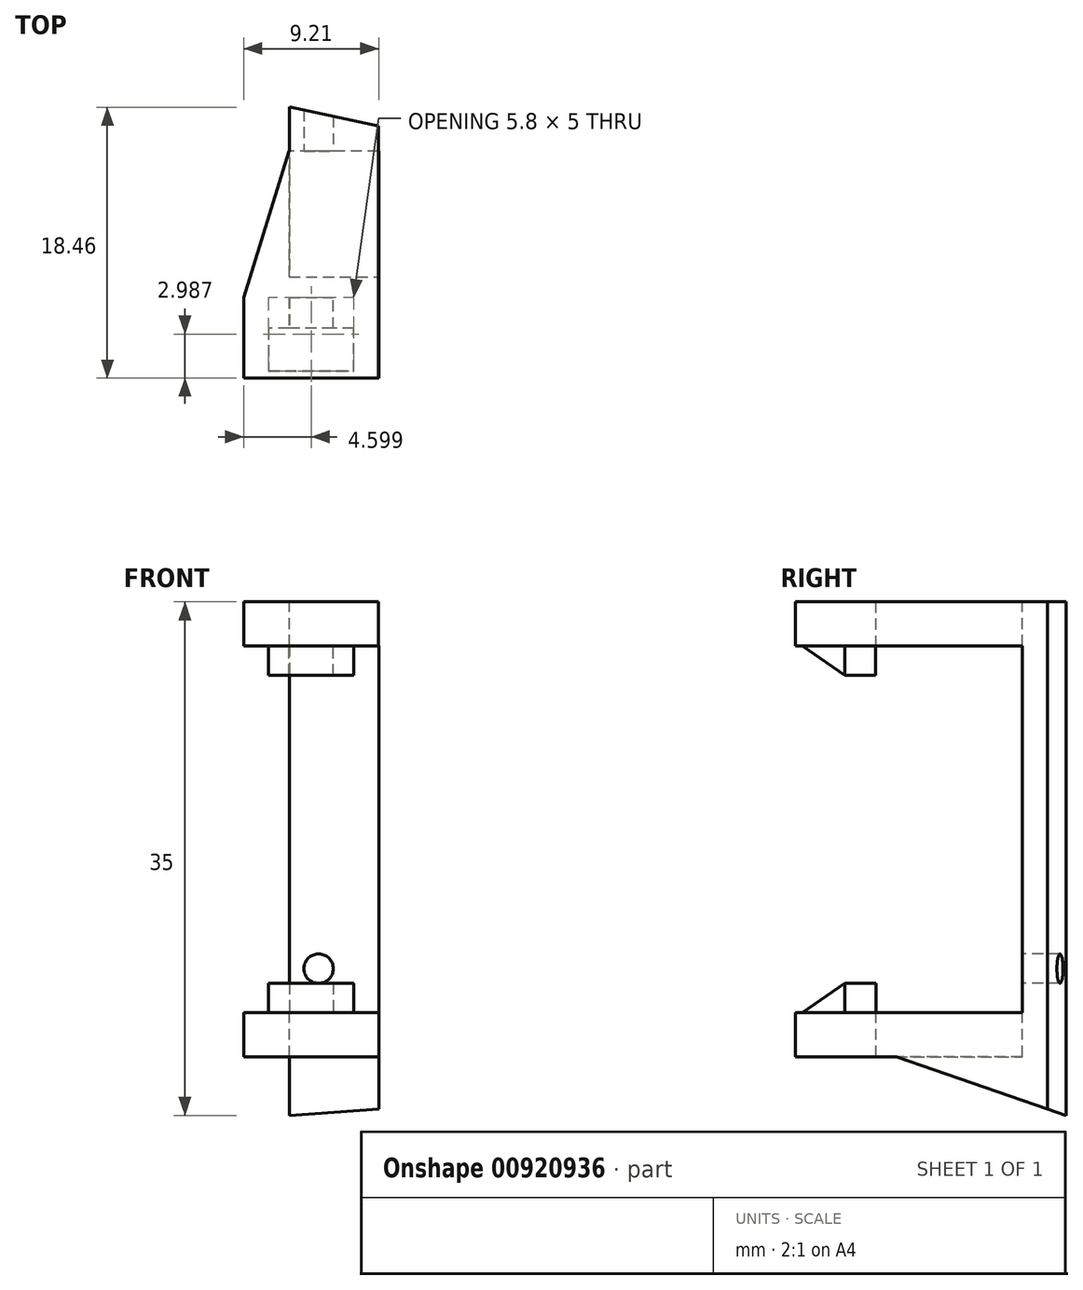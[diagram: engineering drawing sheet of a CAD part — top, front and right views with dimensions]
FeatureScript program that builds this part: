
annotation { "Feature Type Name" : "Feature", "Feature Type Description" : "" }
export const myFeature = defineFeature(function(context is Context, id is Id, definition is map)
    precondition{}
    {
        {
            var Q0;
            Q0=qCreatedBy(makeId("Top.planeOp"),FACE);
            var sketch = newSketch(context, id + "F0", { "sketchPlane" : qUnion([Q0])});
            skLineSegment(sketch, "E0", {"start": v(-27.76, 10.42) * mm, "end": v(-27.76, 8.32) * mm});
            skLineSegment(sketch, "E1", {"start": v(-27.76, 8.32) * mm, "end": v(-29.16, 8.32) * mm});
            skLineSegment(sketch, "E2", {"start": v(-29.16, 8.32) * mm, "end": v(-29.16, 5.42) * mm});
            skLineSegment(sketch, "E3", {"start": v(-29.16, 5.42) * mm, "end": v(-23.36, 5.42) * mm});
            skLineSegment(sketch, "E4", {"start": v(-23.36, 5.42) * mm, "end": v(-23.36, 8.32) * mm});
            skLineSegment(sketch, "E5", {"start": v(-23.36, 8.32) * mm, "end": v(-24.76, 8.32) * mm});
            skLineSegment(sketch, "E6", {"start": v(-24.76, 8.32) * mm, "end": v(-24.76, 10.42) * mm});
            skLineSegment(sketch, "E7", {"start": v(-21.66, 4.93) * mm, "end": v(-21.66, 23.4) * mm});
            skLineSegment(sketch, "E8", {"start": v(-21.66, 23.4) * mm, "end": v(-27.76, 23.4) * mm});
            skLineSegment(sketch, "E9", {"start": v(-30.86, 10.42) * mm, "end": v(-30.86, 4.93) * mm});
            skPoint(sketch, "E10.start.orphan", {"position": v(-27.76, 16.38) * mm});
            skLineSegment(sketch, "E11", {"start": v(-27.76, 10.42) * mm, "end": v(-24.76, 10.42) * mm});
            skLineSegment(sketch, "E12", {"start": v(-30.86, 6.77) * mm, "end": v(-29.16, 6.77) * mm, "construction": true});
            skLineSegment(sketch, "E13", {"start": v(-21.66, 6.9) * mm, "end": v(-23.36, 6.9) * mm, "construction": true});
            skLineSegment(sketch, "E14", {"start": v(-27.76, 23.4) * mm, "end": v(-27.76, 20.4) * mm});
            skLineSegment(sketch, "E15", {"start": v(-27.76, 20.4) * mm, "end": v(-30.86, 10.42) * mm});
            skLineSegment(sketch, "E16", {"start": v(-21.66, 20.4) * mm, "end": v(-27.76, 20.4) * mm});
            skLineSegment(sketch, "E17", {"start": v(-24.1, 20.4) * mm, "end": v(-24.1, 23.4) * mm, "construction": true});
            skLineSegment(sketch, "E18", {"start": v(-25.84, 10.42) * mm, "end": v(-25.84, 20.4) * mm, "construction": true});
            skPoint(sketch, "E19.start.orphan", {"position": v(-30.7, 4.93) * mm});
            skLineSegment(sketch, "E20", {"start": v(-30.86, 4.93) * mm, "end": v(-21.66, 4.93) * mm});
            skSolve(sketch);
        }
        {
            var Q0;
            {var subQ0=sQuery(id+"F0.wireOp",EDGE,"E8");Q0=makeQuery(id+"F0.imprint","IMPRINT",FACE,{"disambiguationData":[TD([[makeQuery(id+"F0.imprint","IMPRINT",EDGE,{"derivedFrom":subQ0}),1.0]])]});}
            extrude(context, id + "F1", {"entities" : qUnion([Q0]), "depth" : 25 * mm, "offsetDistance" : 25 * mm});
        }
        {
            var Q0;
            Q0=makeQuery(id+"F1.opExtrude","CAP_FACE",FACE,{"disambiguationData":[OSD([sQuery(id+"F0.wireOp",EDGE,"E7"),sQuery(id+"F0.wireOp",EDGE,"E8"),sQuery(id+"F0.wireOp",EDGE,"E14"),sQuery(id+"F0.wireOp",EDGE,"E16")])],"isStart":false});
            var sketch = newSketch(context, id + "F2", { "sketchPlane" : qUnion([Q0])});
            skLineSegment(sketch, "E21", {"start": v(-27.77, 10.42) * mm, "end": v(-27.77, 8.32) * mm});
            skLineSegment(sketch, "E22", {"start": v(-27.77, 8.32) * mm, "end": v(-29.17, 8.32) * mm});
            skLineSegment(sketch, "E23", {"start": v(-29.17, 8.32) * mm, "end": v(-29.17, 5.42) * mm});
            skLineSegment(sketch, "E24", {"start": v(-29.17, 5.42) * mm, "end": v(-23.37, 5.42) * mm});
            skLineSegment(sketch, "E25", {"start": v(-23.37, 5.42) * mm, "end": v(-23.37, 8.32) * mm});
            skLineSegment(sketch, "E26", {"start": v(-23.37, 8.32) * mm, "end": v(-24.77, 8.32) * mm});
            skLineSegment(sketch, "E27", {"start": v(-24.77, 8.32) * mm, "end": v(-24.77, 10.42) * mm});
            skLineSegment(sketch, "E28", {"start": v(-21.67, 4.93) * mm, "end": v(-21.67, 23.4) * mm});
            skLineSegment(sketch, "E29", {"start": v(-21.67, 23.4) * mm, "end": v(-27.77, 23.4) * mm});
            skLineSegment(sketch, "E30", {"start": v(-30.87, 10.42) * mm, "end": v(-30.87, 4.93) * mm});
            skPoint(sketch, "E31.start.orphan", {"position": v(-27.77, 16.38) * mm});
            skLineSegment(sketch, "E32", {"start": v(-27.77, 10.42) * mm, "end": v(-24.77, 10.42) * mm});
            skLineSegment(sketch, "E33", {"start": v(-30.87, 6.76) * mm, "end": v(-29.17, 6.76) * mm, "construction": true});
            skLineSegment(sketch, "E34", {"start": v(-21.67, 6.9) * mm, "end": v(-23.37, 6.9) * mm, "construction": true});
            skLineSegment(sketch, "E35", {"start": v(-27.77, 23.4) * mm, "end": v(-27.77, 20.4) * mm});
            skLineSegment(sketch, "E36", {"start": v(-27.77, 20.4) * mm, "end": v(-30.87, 10.42) * mm});
            skLineSegment(sketch, "E37", {"start": v(-21.67, 20.4) * mm, "end": v(-27.77, 20.4) * mm});
            skLineSegment(sketch, "E38", {"start": v(-24.12, 20.4) * mm, "end": v(-24.12, 23.4) * mm, "construction": true});
            skLineSegment(sketch, "E39", {"start": v(-25.85, 10.42) * mm, "end": v(-25.85, 20.4) * mm, "construction": true});
            skPoint(sketch, "E40.end.orphan", {"position": v(-30.7, 4.93) * mm});
            skLineSegment(sketch, "E41", {"start": v(-30.87, 4.93) * mm, "end": v(-21.67, 4.93) * mm});
            skSolve(sketch);
        }
        {
            var Q0;
            Q0=makeQuery(id+"F2.imprint","IMPRINT",FACE,{"disambiguationData":[TD([[makeQuery(id+"F2.imprint","IMPRINT",EDGE,{"derivedFrom":sQuery(id+"F2.wireOp",EDGE,"E21")}),-1.0]])]});
            var Q1;
            {var subQ0=sQuery(id+"F2.wireOp",EDGE,"E29");var subQ1=sQuery(id+"F2.wireOp",EDGE,"E28");var subQ2=makeQuery(id+"F2.imprint","INTERSECT",VERTEX,{"derivedFrom":[subQ1,subQ0]});Q1=makeQuery(id+"F2.imprint","IMPRINT",FACE,{"disambiguationData":[TD([[makeQuery(id+"F2.imprint","IMPRINT",EDGE,{"disambiguationData":[TD([[subQ2,1.0]])],"derivedFrom":subQ1}),1.0]])]});}
            var Q2;
            Q2=makeQuery(id+"F2.imprint","IMPRINT",FACE,{"disambiguationData":[TD([[makeQuery(id+"F2.imprint","IMPRINT",EDGE,{"derivedFrom":sQuery(id+"F2.wireOp",EDGE,"E21")}),1.0]])]});
            extrude(context, id + "F3", {"entities" : qUnion([Q0, Q1, Q2]), "operationType" : NewBodyOperationType.ADD, "depth" : 3 * mm, "offsetDistance" : 25 * mm});
        }
        {
            var Q0;
            Q0=makeQuery(id+"F2.imprint","IMPRINT",FACE,{"disambiguationData":[TD([[makeQuery(id+"F2.imprint","IMPRINT",EDGE,{"derivedFrom":sQuery(id+"F2.wireOp",EDGE,"E21")}),1.0]])]});
            extrude(context, id + "F4", {"entities" : qUnion([Q0]), "operationType" : NewBodyOperationType.ADD, "oppositeDirection" : true, "depth" : 2 * mm, "offsetDistance" : 25 * mm});
        }
        {
            var Q0;
            Q0=makeQuery(id+"F0.imprint","IMPRINT",FACE,{"disambiguationData":[TD([[makeQuery(id+"F0.imprint","IMPRINT",EDGE,{"derivedFrom":sQuery(id+"F0.wireOp",EDGE,"E0")}),-1.0]])]});
            var Q1;
            {var subQ0=sQuery(id+"F0.wireOp",EDGE,"E8");Q1=makeQuery(id+"F0.imprint","IMPRINT",FACE,{"disambiguationData":[TD([[makeQuery(id+"F0.imprint","IMPRINT",EDGE,{"derivedFrom":subQ0}),1.0]])]});}
            var Q2;
            Q2=makeQuery(id+"F0.imprint","IMPRINT",FACE,{"disambiguationData":[TD([[makeQuery(id+"F0.imprint","IMPRINT",EDGE,{"derivedFrom":sQuery(id+"F0.wireOp",EDGE,"E0")}),1.0]])]});
            extrude(context, id + "F5", {"entities" : qUnion([Q0, Q1, Q2]), "operationType" : NewBodyOperationType.ADD, "oppositeDirection" : true, "depth" : 3 * mm, "offsetDistance" : 25 * mm});
        }
        {
            var Q0;
            Q0=makeQuery(id+"F0.imprint","IMPRINT",FACE,{"disambiguationData":[TD([[makeQuery(id+"F0.imprint","IMPRINT",EDGE,{"derivedFrom":sQuery(id+"F0.wireOp",EDGE,"E0")}),1.0]])]});
            extrude(context, id + "F6", {"entities" : qUnion([Q0]), "operationType" : NewBodyOperationType.ADD, "depth" : 2 * mm, "offsetDistance" : 25 * mm});
        }
        {
            var Q0;
            Q0=makeQuery(id+"F6.opExtrude","SWEPT_FACE",FACE,{"disambiguationData":[OSD([sQuery(id+"F0.wireOp",EDGE,"E2")])]});
            var sketch = newSketch(context, id + "F7", { "sketchPlane" : qUnion([Q0])});
            skLineSegment(sketch, "E42", {"start": v(-8.32, 2) * mm, "end": v(-5.42, 0) * mm});
            skLineSegment(sketch, "E43", {"start": v(-5.42, 0) * mm, "end": v(-5.42, 2) * mm});
            skLineSegment(sketch, "E44", {"start": v(-5.42, 2) * mm, "end": v(-8.32, 2) * mm});
            skSolve(sketch);
        }
        {
            var Q0;
            Q0=makeQuery(id+"F4.opExtrude","SWEPT_FACE",FACE,{"disambiguationData":[OSD([sQuery(id+"F2.wireOp",EDGE,"E23")])]});
            var sketch = newSketch(context, id + "F8", { "sketchPlane" : qUnion([Q0])});
            skLineSegment(sketch, "E45", {"start": v(-8.32, 23) * mm, "end": v(-5.42, 23) * mm});
            skLineSegment(sketch, "E46", {"start": v(-5.42, 23) * mm, "end": v(-5.42, 25) * mm});
            skLineSegment(sketch, "E47", {"start": v(-5.42, 25) * mm, "end": v(-8.32, 23) * mm});
            skSolve(sketch);
        }
        {
            var Q0;
            Q0=makeQuery(id+"F7.imprint","IMPRINT",FACE,{"disambiguationData":[TD([[makeQuery(id+"F7.imprint","IMPRINT",EDGE,{"derivedFrom":sQuery(id+"F7.wireOp",EDGE,"E42")}),1.0]])]});
            extrude(context, id + "F9", {"entities" : qUnion([Q0]), "operationType" : NewBodyOperationType.REMOVE, "oppositeDirection" : true, "depth" : 25 * mm, "offsetDistance" : 25 * mm});
        }
        {
            var Q0;
            Q0=makeQuery(id+"F8.imprint","IMPRINT",FACE,{"disambiguationData":[TD([[makeQuery(id+"F8.imprint","IMPRINT",EDGE,{"derivedFrom":sQuery(id+"F8.wireOp",EDGE,"E45")}),1.0]])]});
            extrude(context, id + "F10", {"entities" : qUnion([Q0]), "operationType" : NewBodyOperationType.REMOVE, "oppositeDirection" : true, "depth" : 25 * mm, "offsetDistance" : 25 * mm});
        }
        {
            var Q0;
            {var subQ0=sQuery(id+"F0.wireOp",EDGE,"E7");Q0=makeQuery(id+"F5.boolean.opBoolean","MERGE",FACE,{"derivedFrom":[makeQuery(id+"F1.opExtrude","SWEPT_FACE",FACE,{"disambiguationData":[OSD([subQ0])]}),makeQuery(id+"F5.opExtrude","SWEPT_FACE",FACE,{"disambiguationData":[OSD([subQ0])]})]});}
            var sketch = newSketch(context, id + "F11", { "sketchPlane" : qUnion([Q0])});
            skLineSegment(sketch, "E48", {"start": v(23.4, -3) * mm, "end": v(23.4, -7) * mm});
            skLineSegment(sketch, "E49", {"start": v(23.4, -7) * mm, "end": v(11.82, -3) * mm});
            skLineSegment(sketch, "E50", {"start": v(11.82, -3) * mm, "end": v(23.4, -3) * mm});
            skSolve(sketch);
        }
        {
            var Q0;
            Q0=makeQuery(id+"F11.imprint","IMPRINT",FACE,{"disambiguationData":[TD([[makeQuery(id+"F11.imprint","IMPRINT",EDGE,{"derivedFrom":sQuery(id+"F11.wireOp",EDGE,"E48")}),-1.0]])]});
            extrude(context, id + "F12", {"entities" : qUnion([Q0]), "operationType" : NewBodyOperationType.ADD, "oppositeDirection" : true, "depth" : 6.1 * mm, "offsetDistance" : 25 * mm});
        }
        {
            var Q0;
            {var subQ0=sQuery(id+"F2.wireOp",EDGE,"E28");Q0=makeQuery(id+"F3.boolean.opBoolean","MERGE",FACE,{"derivedFrom":[makeQuery(id+"F3.opExtrude","CAP_FACE",FACE,{"disambiguationData":[OSD([subQ0,sQuery(id+"F2.wireOp",EDGE,"E30"),sQuery(id+"F2.wireOp",EDGE,"E36"),sQuery(id+"F2.wireOp",EDGE,"E37"),sQuery(id+"F2.wireOp",EDGE,"E41")])],"isStart":false}),makeQuery(id+"F3.opExtrude","CAP_FACE",FACE,{"disambiguationData":[OSD([sQuery(id+"F0.wireOp",EDGE,"E14"),sQuery(id+"F0.wireOp",EDGE,"E16"),subQ0,sQuery(id+"F2.wireOp",EDGE,"E29")])],"isStart":false})]});}
            var sketch = newSketch(context, id + "F13", { "sketchPlane" : qUnion([Q0])});
            skLineSegment(sketch, "E51", {"start": v(-27.76, 23.4) * mm, "end": v(-21.67, 22.11) * mm});
            skLineSegment(sketch, "E52", {"start": v(-21.67, 22.11) * mm, "end": v(-21.67, 23.4) * mm});
            skLineSegment(sketch, "E53", {"start": v(-21.67, 23.4) * mm, "end": v(-27.76, 23.4) * mm});
            skSolve(sketch);
        }
        {
            var Q0;
            Q0=makeQuery(id+"F13.imprint","IMPRINT",FACE,{"disambiguationData":[TD([[makeQuery(id+"F13.imprint","IMPRINT",EDGE,{"derivedFrom":sQuery(id+"F13.wireOp",EDGE,"E51")}),1.0]])]});
            extrude(context, id + "F14", {"entities" : qUnion([Q0]), "operationType" : NewBodyOperationType.REMOVE, "oppositeDirection" : true, "depth" : 37.75 * mm, "offsetDistance" : 25 * mm});
        }
        {
            var Q0;
            Q0=makeQuery(id+"F1.opExtrude","SWEPT_FACE",FACE,{"disambiguationData":[OSD([sQuery(id+"F0.wireOp",EDGE,"E16")])]});
            var sketch = newSketch(context, id + "F15", { "sketchPlane" : qUnion([Q0])});
            skLineSegment(sketch, "E54", {"start": v(-25.76, 0) * mm, "end": v(-25.76, 3) * mm, "construction": true});
            skLineSegment(sketch, "E55", {"start": v(-25.76, 3) * mm, "end": v(-27.76, 3) * mm, "construction": true});
            skCircle(sketch, "E56", {"center": v(-25.76, 3) * mm, "radius": 1 * mm});
            skSolve(sketch);
        }
        {
            var Q0;
            Q0=makeQuery(id+"F15.imprint","IMPRINT",FACE,{"disambiguationData":[TD([[makeQuery(id+"F15.imprint","IMPRINT",EDGE,{"derivedFrom":sQuery(id+"F15.wireOp",EDGE,"E56")}),1.0]])]});
            extrude(context, id + "F16", {"entities" : qUnion([Q0]), "operationType" : NewBodyOperationType.REMOVE, "oppositeDirection" : true, "depth" : 25 * mm, "offsetDistance" : 25 * mm});
        }
    });
